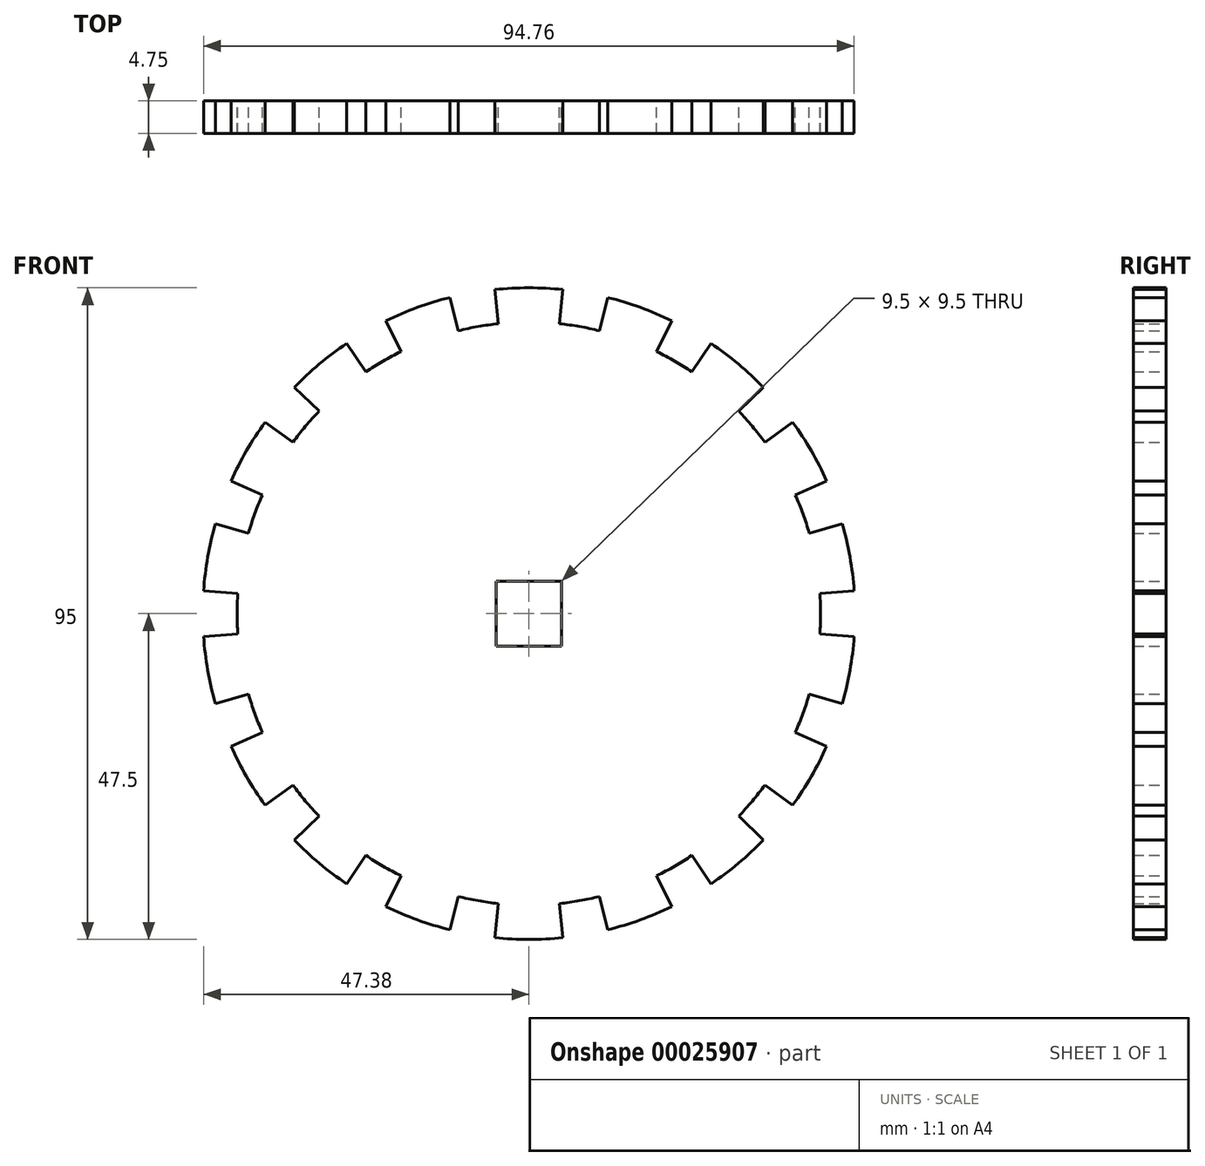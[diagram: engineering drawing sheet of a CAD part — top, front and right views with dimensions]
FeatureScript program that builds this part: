
annotation { "Feature Type Name" : "Feature", "Feature Type Description" : "" }
export const myFeature = defineFeature(function(context is Context, id is Id, definition is map)
    precondition{}
    {
        {
            var Q0;
            Q0=qCreatedBy(makeId("Front.planeOp"),FACE);
            var sketch = newSketch(context, id + "F0", { "sketchPlane" : qUnion([Q0])});
            skCircle(sketch, "E0", {"center": v(0, 0) * mm, "radius": 47.5 * mm, "construction": true});
            skCircle(sketch, "E1", {"center": v(0, 0) * mm, "radius": 42.5 * mm, "construction": true});
            skLineSegment(sketch, "E2", {"start": v(-4.97, 47.24) * mm, "end": v(0, 0) * mm, "construction": true});
            skLineSegment(sketch, "E3", {"start": v(0, 0) * mm, "end": v(-8.25, 46.78) * mm, "construction": true});
            skArc(sketch, "E4", {"start": v(-7.38, 41.85) * mm, "mid": v(-5.91, 42.09) * mm, "end": v(-4.44, 42.27) * mm});
            skLineSegment(sketch, "E5", {"start": v(-4.44, 42.27) * mm, "end": v(-4.97, 47.24) * mm});
            skArc(sketch, "E6", {"start": v(-4.97, 47.24) * mm, "mid": v(-2.49, 47.43) * mm, "end": v(0, 47.5) * mm});
            skArc(sketch, "E7.MirrorCS", {"start": v(4.97, 47.24) * mm, "mid": v(2.49, 47.43) * mm, "end": v(0, 47.5) * mm});
            skLineSegment(sketch, "E8.MirrorCS", {"start": v(4.44, 42.27) * mm, "end": v(4.97, 47.24) * mm});
            skArc(sketch, "E9.MirrorCS", {"start": v(7.38, 41.85) * mm, "mid": v(5.91, 42.09) * mm, "end": v(4.44, 42.27) * mm});
            skArc(sketch, "E10.1.0", {"start": v(-21.25, 36.8) * mm, "mid": v(-19.95, 37.53) * mm, "end": v(-18.63, 38.2) * mm});
            skLineSegment(sketch, "E10.1.1", {"start": v(-18.63, 38.2) * mm, "end": v(-20.82, 42.7) * mm});
            skArc(sketch, "E10.1.2", {"start": v(-20.82, 42.7) * mm, "mid": v(-18.56, 43.72) * mm, "end": v(-16.25, 44.64) * mm});
            skArc(sketch, "E10.1.3", {"start": v(-11.5, 46.09) * mm, "mid": v(-13.89, 45.42) * mm, "end": v(-16.25, 44.64) * mm});
            skLineSegment(sketch, "E10.1.4", {"start": v(-10.28, 41.24) * mm, "end": v(-11.5, 46.09) * mm});
            skArc(sketch, "E10.1.5", {"start": v(-7.38, 41.85) * mm, "mid": v(-8.84, 41.57) * mm, "end": v(-10.28, 41.24) * mm});
            skArc(sketch, "E10.2.0", {"start": v(-32.56, 27.32) * mm, "mid": v(-31.58, 28.44) * mm, "end": v(-30.57, 29.52) * mm});
            skLineSegment(sketch, "E10.2.1", {"start": v(-30.57, 29.52) * mm, "end": v(-34.17, 33) * mm});
            skArc(sketch, "E10.2.2", {"start": v(-34.17, 33) * mm, "mid": v(-32.4, 34.74) * mm, "end": v(-30.53, 36.39) * mm});
            skArc(sketch, "E10.2.3", {"start": v(-26.56, 39.38) * mm, "mid": v(-28.59, 37.94) * mm, "end": v(-30.53, 36.39) * mm});
            skLineSegment(sketch, "E10.2.4", {"start": v(-23.77, 35.23) * mm, "end": v(-26.56, 39.38) * mm});
            skArc(sketch, "E10.2.5", {"start": v(-21.25, 36.8) * mm, "mid": v(-22.52, 36.04) * mm, "end": v(-23.77, 35.23) * mm});
            skArc(sketch, "E10.3.0", {"start": v(-39.94, 14.54) * mm, "mid": v(-39.4, 15.92) * mm, "end": v(-38.83, 17.29) * mm});
            skLineSegment(sketch, "E10.3.1", {"start": v(-38.83, 17.29) * mm, "end": v(-43.4, 19.32) * mm});
            skArc(sketch, "E10.3.2", {"start": v(-43.4, 19.32) * mm, "mid": v(-42.32, 21.56) * mm, "end": v(-41.14, 23.75) * mm});
            skArc(sketch, "E10.3.3", {"start": v(-38.43, 27.92) * mm, "mid": v(-39.84, 25.87) * mm, "end": v(-41.14, 23.75) * mm});
            skLineSegment(sketch, "E10.3.4", {"start": v(-34.38, 24.98) * mm, "end": v(-38.43, 27.92) * mm});
            skArc(sketch, "E10.3.5", {"start": v(-32.56, 27.32) * mm, "mid": v(-33.5, 26.17) * mm, "end": v(-34.38, 24.98) * mm});
            skArc(sketch, "E10.4.0", {"start": v(-42.5, 0) * mm, "mid": v(-42.47, 1.48) * mm, "end": v(-42.4, 2.96) * mm});
            skLineSegment(sketch, "E10.4.1", {"start": v(-42.4, 2.96) * mm, "end": v(-47.38, 3.31) * mm});
            skArc(sketch, "E10.4.2", {"start": v(-47.38, 3.31) * mm, "mid": v(-47.15, 5.79) * mm, "end": v(-46.78, 8.25) * mm});
            skArc(sketch, "E10.4.3", {"start": v(-45.66, 13.1) * mm, "mid": v(-46.28, 10.69) * mm, "end": v(-46.78, 8.25) * mm});
            skLineSegment(sketch, "E10.4.4", {"start": v(-40.85, 11.71) * mm, "end": v(-45.66, 13.1) * mm});
            skArc(sketch, "E10.4.5", {"start": v(-39.94, 14.54) * mm, "mid": v(-40.42, 13.13) * mm, "end": v(-40.85, 11.71) * mm});
            skArc(sketch, "E10.5.0", {"start": v(-39.94, -14.54) * mm, "mid": v(-40.42, -13.13) * mm, "end": v(-40.85, -11.71) * mm});
            skLineSegment(sketch, "E10.5.1", {"start": v(-40.85, -11.71) * mm, "end": v(-45.66, -13.1) * mm});
            skArc(sketch, "E10.5.2", {"start": v(-45.66, -13.1) * mm, "mid": v(-46.28, -10.69) * mm, "end": v(-46.78, -8.25) * mm});
            skArc(sketch, "E10.5.3", {"start": v(-47.38, -3.31) * mm, "mid": v(-47.15, -5.79) * mm, "end": v(-46.78, -8.25) * mm});
            skLineSegment(sketch, "E10.5.4", {"start": v(-42.4, -2.96) * mm, "end": v(-47.38, -3.31) * mm});
            skArc(sketch, "E10.5.5", {"start": v(-42.5, 0) * mm, "mid": v(-42.47, -1.48) * mm, "end": v(-42.4, -2.96) * mm});
            skArc(sketch, "E10.6.0", {"start": v(-32.56, -27.32) * mm, "mid": v(-33.5, -26.17) * mm, "end": v(-34.38, -24.98) * mm});
            skLineSegment(sketch, "E10.6.1", {"start": v(-34.38, -24.98) * mm, "end": v(-38.43, -27.92) * mm});
            skArc(sketch, "E10.6.2", {"start": v(-38.43, -27.92) * mm, "mid": v(-39.84, -25.87) * mm, "end": v(-41.14, -23.75) * mm});
            skArc(sketch, "E10.6.3", {"start": v(-43.4, -19.32) * mm, "mid": v(-42.32, -21.56) * mm, "end": v(-41.14, -23.75) * mm});
            skLineSegment(sketch, "E10.6.4", {"start": v(-38.83, -17.29) * mm, "end": v(-43.4, -19.32) * mm});
            skArc(sketch, "E10.6.5", {"start": v(-39.94, -14.54) * mm, "mid": v(-39.4, -15.92) * mm, "end": v(-38.83, -17.29) * mm});
            skArc(sketch, "E10.7.0", {"start": v(-21.25, -36.8) * mm, "mid": v(-22.52, -36.04) * mm, "end": v(-23.77, -35.23) * mm});
            skLineSegment(sketch, "E10.7.1", {"start": v(-23.77, -35.23) * mm, "end": v(-26.56, -39.38) * mm});
            skArc(sketch, "E10.7.2", {"start": v(-26.56, -39.38) * mm, "mid": v(-28.59, -37.94) * mm, "end": v(-30.53, -36.39) * mm});
            skArc(sketch, "E10.7.3", {"start": v(-34.17, -33) * mm, "mid": v(-32.4, -34.74) * mm, "end": v(-30.53, -36.39) * mm});
            skLineSegment(sketch, "E10.7.4", {"start": v(-30.57, -29.52) * mm, "end": v(-34.17, -33) * mm});
            skArc(sketch, "E10.7.5", {"start": v(-32.56, -27.32) * mm, "mid": v(-31.58, -28.44) * mm, "end": v(-30.57, -29.52) * mm});
            skArc(sketch, "E10.8.0", {"start": v(-7.38, -41.85) * mm, "mid": v(-8.84, -41.57) * mm, "end": v(-10.28, -41.24) * mm});
            skLineSegment(sketch, "E10.8.1", {"start": v(-10.28, -41.24) * mm, "end": v(-11.5, -46.09) * mm});
            skArc(sketch, "E10.8.2", {"start": v(-11.5, -46.09) * mm, "mid": v(-13.89, -45.42) * mm, "end": v(-16.25, -44.64) * mm});
            skArc(sketch, "E10.8.3", {"start": v(-20.82, -42.7) * mm, "mid": v(-18.56, -43.72) * mm, "end": v(-16.25, -44.64) * mm});
            skLineSegment(sketch, "E10.8.4", {"start": v(-18.63, -38.2) * mm, "end": v(-20.82, -42.7) * mm});
            skArc(sketch, "E10.8.5", {"start": v(-21.25, -36.8) * mm, "mid": v(-19.95, -37.53) * mm, "end": v(-18.63, -38.2) * mm});
            skArc(sketch, "E10.9.0", {"start": v(7.38, -41.85) * mm, "mid": v(5.91, -42.09) * mm, "end": v(4.44, -42.27) * mm});
            skLineSegment(sketch, "E10.9.1", {"start": v(4.44, -42.27) * mm, "end": v(4.97, -47.24) * mm});
            skArc(sketch, "E10.9.2", {"start": v(4.97, -47.24) * mm, "mid": v(2.49, -47.43) * mm, "end": v(0, -47.5) * mm});
            skArc(sketch, "E10.9.3", {"start": v(-4.97, -47.24) * mm, "mid": v(-2.49, -47.43) * mm, "end": v(0, -47.5) * mm});
            skLineSegment(sketch, "E10.9.4", {"start": v(-4.44, -42.27) * mm, "end": v(-4.97, -47.24) * mm});
            skArc(sketch, "E10.9.5", {"start": v(-7.38, -41.85) * mm, "mid": v(-5.91, -42.09) * mm, "end": v(-4.44, -42.27) * mm});
            skArc(sketch, "E10.10.0", {"start": v(21.25, -36.8) * mm, "mid": v(19.95, -37.53) * mm, "end": v(18.63, -38.2) * mm});
            skLineSegment(sketch, "E10.10.1", {"start": v(18.63, -38.2) * mm, "end": v(20.82, -42.7) * mm});
            skArc(sketch, "E10.10.2", {"start": v(20.82, -42.7) * mm, "mid": v(18.56, -43.72) * mm, "end": v(16.25, -44.64) * mm});
            skArc(sketch, "E10.10.3", {"start": v(11.5, -46.09) * mm, "mid": v(13.89, -45.42) * mm, "end": v(16.25, -44.64) * mm});
            skLineSegment(sketch, "E10.10.4", {"start": v(10.28, -41.24) * mm, "end": v(11.5, -46.09) * mm});
            skArc(sketch, "E10.10.5", {"start": v(7.38, -41.85) * mm, "mid": v(8.84, -41.57) * mm, "end": v(10.28, -41.24) * mm});
            skArc(sketch, "E10.11.0", {"start": v(32.56, -27.32) * mm, "mid": v(31.58, -28.44) * mm, "end": v(30.57, -29.52) * mm});
            skLineSegment(sketch, "E10.11.1", {"start": v(30.57, -29.52) * mm, "end": v(34.17, -33) * mm});
            skArc(sketch, "E10.11.2", {"start": v(34.17, -33) * mm, "mid": v(32.4, -34.74) * mm, "end": v(30.53, -36.39) * mm});
            skArc(sketch, "E10.11.3", {"start": v(26.56, -39.38) * mm, "mid": v(28.59, -37.94) * mm, "end": v(30.53, -36.39) * mm});
            skLineSegment(sketch, "E10.11.4", {"start": v(23.77, -35.23) * mm, "end": v(26.56, -39.38) * mm});
            skArc(sketch, "E10.11.5", {"start": v(21.25, -36.8) * mm, "mid": v(22.52, -36.04) * mm, "end": v(23.77, -35.23) * mm});
            skArc(sketch, "E10.12.0", {"start": v(39.94, -14.54) * mm, "mid": v(39.4, -15.92) * mm, "end": v(38.83, -17.29) * mm});
            skLineSegment(sketch, "E10.12.1", {"start": v(38.83, -17.29) * mm, "end": v(43.4, -19.32) * mm});
            skArc(sketch, "E10.12.2", {"start": v(43.4, -19.32) * mm, "mid": v(42.32, -21.56) * mm, "end": v(41.14, -23.75) * mm});
            skArc(sketch, "E10.12.3", {"start": v(38.43, -27.92) * mm, "mid": v(39.84, -25.87) * mm, "end": v(41.14, -23.75) * mm});
            skLineSegment(sketch, "E10.12.4", {"start": v(34.38, -24.98) * mm, "end": v(38.43, -27.92) * mm});
            skArc(sketch, "E10.12.5", {"start": v(32.56, -27.32) * mm, "mid": v(33.5, -26.17) * mm, "end": v(34.38, -24.98) * mm});
            skArc(sketch, "E10.13.0", {"start": v(42.5, 0) * mm, "mid": v(42.47, -1.48) * mm, "end": v(42.4, -2.96) * mm});
            skLineSegment(sketch, "E10.13.1", {"start": v(42.4, -2.96) * mm, "end": v(47.38, -3.31) * mm});
            skArc(sketch, "E10.13.2", {"start": v(47.38, -3.31) * mm, "mid": v(47.15, -5.79) * mm, "end": v(46.78, -8.25) * mm});
            skArc(sketch, "E10.13.3", {"start": v(45.66, -13.1) * mm, "mid": v(46.28, -10.69) * mm, "end": v(46.78, -8.25) * mm});
            skLineSegment(sketch, "E10.13.4", {"start": v(40.85, -11.71) * mm, "end": v(45.66, -13.1) * mm});
            skArc(sketch, "E10.13.5", {"start": v(39.94, -14.54) * mm, "mid": v(40.42, -13.13) * mm, "end": v(40.85, -11.71) * mm});
            skArc(sketch, "E10.14.0", {"start": v(39.94, 14.54) * mm, "mid": v(40.42, 13.13) * mm, "end": v(40.85, 11.71) * mm});
            skLineSegment(sketch, "E10.14.1", {"start": v(40.85, 11.71) * mm, "end": v(45.66, 13.1) * mm});
            skArc(sketch, "E10.14.2", {"start": v(45.66, 13.1) * mm, "mid": v(46.28, 10.69) * mm, "end": v(46.78, 8.25) * mm});
            skArc(sketch, "E10.14.3", {"start": v(47.38, 3.31) * mm, "mid": v(47.15, 5.79) * mm, "end": v(46.78, 8.25) * mm});
            skLineSegment(sketch, "E10.14.4", {"start": v(42.4, 2.96) * mm, "end": v(47.38, 3.31) * mm});
            skArc(sketch, "E10.14.5", {"start": v(42.5, 0) * mm, "mid": v(42.47, 1.48) * mm, "end": v(42.4, 2.96) * mm});
            skArc(sketch, "E10.15.0", {"start": v(32.56, 27.32) * mm, "mid": v(33.5, 26.17) * mm, "end": v(34.38, 24.98) * mm});
            skLineSegment(sketch, "E10.15.1", {"start": v(34.38, 24.98) * mm, "end": v(38.43, 27.92) * mm});
            skArc(sketch, "E10.15.2", {"start": v(38.43, 27.92) * mm, "mid": v(39.84, 25.87) * mm, "end": v(41.14, 23.75) * mm});
            skArc(sketch, "E10.15.3", {"start": v(43.4, 19.32) * mm, "mid": v(42.32, 21.56) * mm, "end": v(41.14, 23.75) * mm});
            skLineSegment(sketch, "E10.15.4", {"start": v(38.83, 17.29) * mm, "end": v(43.4, 19.32) * mm});
            skArc(sketch, "E10.15.5", {"start": v(39.94, 14.54) * mm, "mid": v(39.4, 15.92) * mm, "end": v(38.83, 17.29) * mm});
            skArc(sketch, "E10.16.0", {"start": v(21.25, 36.8) * mm, "mid": v(22.52, 36.04) * mm, "end": v(23.77, 35.23) * mm});
            skLineSegment(sketch, "E10.16.1", {"start": v(23.77, 35.23) * mm, "end": v(26.56, 39.38) * mm});
            skArc(sketch, "E10.16.2", {"start": v(26.56, 39.38) * mm, "mid": v(28.59, 37.94) * mm, "end": v(30.53, 36.39) * mm});
            skArc(sketch, "E10.16.3", {"start": v(34.17, 33) * mm, "mid": v(32.4, 34.74) * mm, "end": v(30.53, 36.39) * mm});
            skLineSegment(sketch, "E10.16.4", {"start": v(30.57, 29.52) * mm, "end": v(34.17, 33) * mm});
            skArc(sketch, "E10.16.5", {"start": v(32.56, 27.32) * mm, "mid": v(31.58, 28.44) * mm, "end": v(30.57, 29.52) * mm});
            skArc(sketch, "E10.17.0", {"start": v(7.38, 41.85) * mm, "mid": v(8.84, 41.57) * mm, "end": v(10.28, 41.24) * mm});
            skLineSegment(sketch, "E10.17.1", {"start": v(10.28, 41.24) * mm, "end": v(11.5, 46.09) * mm});
            skArc(sketch, "E10.17.2", {"start": v(11.5, 46.09) * mm, "mid": v(13.89, 45.42) * mm, "end": v(16.25, 44.64) * mm});
            skArc(sketch, "E10.17.3", {"start": v(20.82, 42.7) * mm, "mid": v(18.56, 43.72) * mm, "end": v(16.25, 44.64) * mm});
            skLineSegment(sketch, "E10.17.4", {"start": v(18.63, 38.2) * mm, "end": v(20.82, 42.7) * mm});
            skArc(sketch, "E10.17.5", {"start": v(21.25, 36.8) * mm, "mid": v(19.95, 37.53) * mm, "end": v(18.63, 38.2) * mm});
            skLineSegment(sketch, "E11.rect.bottom", {"start": v(-4.75, -4.75) * mm, "end": v(4.75, -4.75) * mm});
            skLineSegment(sketch, "E11.rect.top", {"start": v(-4.75, 4.75) * mm, "end": v(4.75, 4.75) * mm});
            skLineSegment(sketch, "E11.rect.left", {"start": v(-4.75, -4.75) * mm, "end": v(-4.75, 4.75) * mm});
            skLineSegment(sketch, "E11.rect.right", {"start": v(4.75, -4.75) * mm, "end": v(4.75, 4.75) * mm});
            skSolve(sketch);
        }
        {
            var Q0;
            Q0 = qSketchRegion(id + "F0", true);
            extrude(context, id + "F1", {"entities" : qUnion([Q0]), "depth" : 4.75 * mm});
        }
    });
